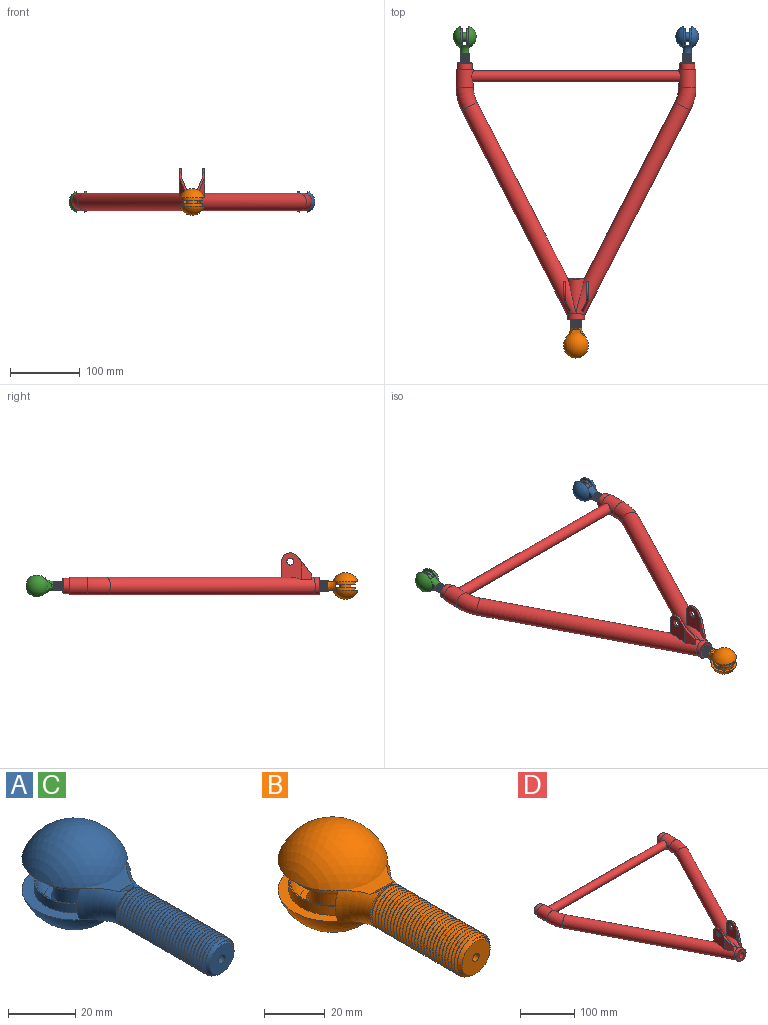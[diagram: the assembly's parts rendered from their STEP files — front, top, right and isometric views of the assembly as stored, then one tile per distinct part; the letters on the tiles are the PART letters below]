
ASSEMBLY  parts=4 mates=7
PART A: 88 faces, bbox 67.8x97.3x67.8 mm
  f0: cylinder r=12.03mm len=24.05mm, axis (0,0,1), area 245.9mm2, adj f1,f87
  f1: plane 30.08x30.08mm, normal (0,0,-1), area 28.6mm2, adj f0,f2
  f2: sphere r=11.91mm, area 421.7mm2, adj f1,f3
  f3: plane 17.75x17.75mm, normal (0,0,-1), area 94.1mm2, adj f2,f4
  f4: cone r=0mm half-angle=45deg, axis (0,0,-1), area 37.6mm2, adj f3,f5
  f5: cylinder r=6.35mm len=14.61mm, axis (0,0,1), area 582.7mm2, adj f4,f6
  f6: cone r=0mm half-angle=45deg, axis (0,0,1), area 37.6mm2, adj f5,f7
  f7: plane 37.19x37.19mm, normal (0,0,1), area 94.1mm2, adj f6,f8
  f8: sphere r=11.91mm, area 718.6mm2, adj f7,f9
  f9: plane 30.08x30.08mm, normal (0,0,1), area 28.6mm2, adj f8,f10
  f10: cylinder r=12.03mm len=24.05mm, axis (0,0,1), area 245.9mm2, adj f9,f11
  f11: plane 37.68x31.81mm, normal (0,0,1), area 376.1mm2, adj f10,f12,f84,f85,f86
  f12: torus R=22.32mm, axis (0,-1,0), area 180.4mm2, adj f11,f13,f15,f84,f86,f87
  f13: plane 6.9x3.09mm, normal (0,0.25,-0.97), area 9.3mm2, adj f12,f14,f87
  f14: torus R=22.32mm, axis (0,-1,0), area 90.2mm2, adj f13,f15,f84,f85,f87
  f15: plane 13.2x13.2mm, normal (0,-1,0), area 15.6mm2, adj f12,f14,f16,f82,f83,f85
  f16: bspline ~38.84x12.7mm, area 1026.5mm2, adj f15,f17,f18,f19,f20,f21,f22,f23
  f17: cylinder r=6.35mm len=12.7mm, axis (0,1,0), area 2.8mm2, adj f16,f18,f83,f85
  f18: cylinder r=6.35mm len=12.7mm, axis (0,1,0), area 3.2mm2, adj f16,f17,f19,f83
  f19: cylinder r=6.35mm len=12.7mm, axis (0,1,0), area 3.2mm2, adj f16,f18,f20,f83
  f20: cylinder r=6.35mm len=12.7mm, axis (0,1,0), area 3.2mm2, adj f16,f19,f21,f83
  f21: cylinder r=6.35mm len=12.7mm, axis (0,1,0), area 3.2mm2, adj f16,f20,f22,f83
  f22: cylinder r=6.35mm len=12.7mm, axis (0,1,0), area 3.2mm2, adj f16,f21,f23,f83
  f23: cylinder r=6.35mm len=12.7mm, axis (0,1,0), area 3.2mm2, adj f16,f22,f24,f83
  f24: cylinder r=6.35mm len=12.7mm, axis (0,1,0), area 3.2mm2, adj f16,f23,f25,f83
  f25: cylinder r=6.35mm len=12.7mm, axis (0,1,0), area 3.2mm2, adj f16,f24,f26,f83
  f26: cylinder r=6.35mm len=12.7mm, axis (0,1,0), area 3.2mm2, adj f16,f25,f27,f83
  f27: cylinder r=6.35mm len=12.7mm, axis (0,1,0), area 3.2mm2, adj f16,f26,f28,f83
  f28: cylinder r=6.35mm len=12.7mm, axis (0,1,0), area 3.2mm2, adj f16,f27,f29,f83
  f29: cylinder r=6.35mm len=12.7mm, axis (0,1,0), area 3.2mm2, adj f16,f28,f30,f83
  f30: cylinder r=6.35mm len=12.7mm, axis (0,1,0), area 3.2mm2, adj f16,f29,f31,f83
  f31: cylinder r=6.35mm len=12.7mm, axis (0,1,0), area 3.2mm2, adj f16,f30,f32,f83
  f32: cylinder r=6.35mm len=12.7mm, axis (0,1,0), area 3.2mm2, adj f16,f31,f33,f83
  f33: cylinder r=6.35mm len=12.7mm, axis (0,1,0), area 3.2mm2, adj f16,f32,f34,f83
  f34: cylinder r=6.35mm len=12.7mm, axis (0,1,0), area 3.2mm2, adj f16,f33,f35,f83
  f35: cylinder r=6.35mm len=12.7mm, axis (0,1,0), area 3.2mm2, adj f16,f34,f36,f83
  f36: cylinder r=6.35mm len=12.7mm, axis (0,1,0), area 3.2mm2, adj f16,f35,f37,f83
  f37: cylinder r=6.35mm len=12.7mm, axis (0,1,0), area 3.2mm2, adj f16,f36,f38,f83
  f38: cylinder r=6.35mm len=12.7mm, axis (0,1,0), area 3.2mm2, adj f16,f37,f39,f83
  f39: cylinder r=6.35mm len=12.7mm, axis (0,1,0), area 3.2mm2, adj f16,f38,f40,f83
  f40: cylinder r=6.35mm len=12.7mm, axis (0,1,0), area 3.2mm2, adj f16,f39,f41,f83
  f41: cylinder r=6.35mm len=12.7mm, axis (0,1,0), area 3.2mm2, adj f16,f40,f42,f83
  f42: cylinder r=6.35mm len=12.7mm, axis (0,1,0), area 3.2mm2, adj f16,f41,f43,f83
  f43: cylinder r=6.35mm len=12.7mm, axis (0,1,0), area 3.2mm2, adj f16,f42,f44,f83
  f44: cylinder r=6.35mm len=12.7mm, axis (0,1,0), area 3.2mm2, adj f16,f43,f45,f83
  f45: cylinder r=6.35mm len=12.7mm, axis (0,1,0), area 3.2mm2, adj f16,f44,f46,f83
  f46: cylinder r=6.35mm len=12.7mm, axis (0,1,0), area 3.2mm2, adj f16,f45,f47,f83
  f47: cylinder r=6.35mm len=12.7mm, axis (0,1,0), area 3.2mm2, adj f16,f46,f48,f83
  f48: cylinder r=6.35mm len=12.7mm, axis (0,1,0), area 3.2mm2, adj f16,f47,f49,f83
  f49: cylinder r=6.35mm len=12.7mm, axis (0,1,0), area 3.2mm2, adj f16,f48,f50,f83
  f50: cylinder r=6.35mm len=12.7mm, axis (0,1,0), area 3.2mm2, adj f16,f49,f51,f83
  f51: cylinder r=6.35mm len=12.7mm, axis (0,1,0), area 3.2mm2, adj f16,f50,f52,f83
  f52: cylinder r=6.35mm len=12.7mm, axis (0,1,0), area 3.2mm2, adj f16,f51,f53,f83
  f53: cylinder r=6.35mm len=12.7mm, axis (0,1,0), area 3.2mm2, adj f16,f52,f54,f83
  f54: cylinder r=6.35mm len=12.7mm, axis (0,1,0), area 3.2mm2, adj f16,f53,f55,f83
  f55: cylinder r=6.35mm len=12.7mm, axis (0,1,0), area 3.2mm2, adj f16,f54,f56,f83
  f56: cylinder r=6.35mm len=12.7mm, axis (0,1,0), area 3.2mm2, adj f16,f55,f57,f83
  f57: cylinder r=6.35mm len=12.7mm, axis (0,1,0), area 3.2mm2, adj f16,f56,f58,f83
  f58: cylinder r=6.35mm len=12.7mm, axis (0,1,0), area 3.2mm2, adj f16,f57,f59,f83
  f59: cylinder r=6.35mm len=12.7mm, axis (0,1,0), area 3.2mm2, adj f16,f58,f60,f83
  f60: cylinder r=6.35mm len=12.7mm, axis (0,1,0), area 3.2mm2, adj f16,f59,f61,f83
  f61: cylinder r=6.35mm len=12.7mm, axis (0,1,0), area 3.2mm2, adj f16,f60,f62,f83
  f62: cylinder r=6.35mm len=12.7mm, axis (0,1,0), area 3.2mm2, adj f16,f61,f63,f83
  f63: cylinder r=6.35mm len=12.7mm, axis (0,1,0), area 3.2mm2, adj f16,f62,f64,f83
  f64: cylinder r=6.35mm len=12.7mm, axis (0,1,0), area 3.2mm2, adj f16,f63,f65,f83
  f65: cylinder r=6.35mm len=12.7mm, axis (0,1,0), area 3.2mm2, adj f16,f64,f66,f83
  f66: cylinder r=6.35mm len=12.7mm, axis (0,1,0), area 3.2mm2, adj f16,f65,f67,f83
  f67: cylinder r=6.35mm len=12.7mm, axis (0,1,0), area 3.2mm2, adj f16,f66,f68,f83
  f68: cylinder r=6.35mm len=12.7mm, axis (0,1,0), area 3.2mm2, adj f16,f67,f69,f83
  f69: cylinder r=6.35mm len=12.7mm, axis (0,1,0), area 3.2mm2, adj f16,f68,f70,f83
  f70: cylinder r=6.35mm len=12.7mm, axis (0,1,0), area 3.2mm2, adj f16,f69,f71,f83
  f71: cylinder r=6.35mm len=12.7mm, axis (0,1,0), area 3.2mm2, adj f16,f70,f72,f83
  f72: cylinder r=6.35mm len=12.7mm, axis (0,1,0), area 3.2mm2, adj f16,f71,f73,f83
  f73: cylinder r=6.35mm len=12.7mm, axis (0,1,0), area 3.2mm2, adj f16,f72,f74,f76,f83
  f74: cylinder r=6.35mm len=12.7mm, axis (0,1,0), area 3.2mm2, adj f73,f75,f76,f83
  f75: cylinder r=6.35mm len=4.49mm, axis (0,1,0), area 0.4mm2, adj f74,f76,f81
  f76: bspline ~14.55x14.53mm, area 18.3mm2, adj f73,f74,f75,f77,f81
  f77: cone r=0mm half-angle=45deg, axis (0,1,0), area 18.6mm2, adj f76,f78,f81
  f78: plane 10.16x10.16mm, normal (0,-1,0), area 74mm2, adj f77,f79,f81
  f79: cylinder r=1.5mm len=15mm, axis (0,-1,0), area 141.4mm2, adj f78,f80
  f80: plane 3x3mm, normal (0,-1,0), area 7.1mm2, adj f79
  f81: cone r=0mm half-angle=45deg, axis (0,1,0), area 23.7mm2, adj f16,f75,f76,f77,f78,f82,f83
  f82: cylinder r=5.53mm len=37.66mm, axis (0,1,0), area 165.1mm2, adj f15,f16,f81,f83
  f83: bspline ~38.26x12.7mm, area 1045.6mm2, adj f15,f17,f18,f19,f20,f21,f22,f23
  f84: sphere r=16.67mm, area 2557.4mm2, adj f11,f12,f14,f85,f87
  f85: torus R=22.32mm, axis (0,-1,0), area 90.2mm2, adj f11,f14,f15,f17,f84,f86
  f86: plane 6.9x3.09mm, normal (0,0.25,0.97), area 9.3mm2, adj f11,f12,f85
  f87: plane 37.68x31.81mm, normal (0,0,-1), area 376.3mm2, adj f0,f12,f13,f14,f84
PART B: 86 faces, bbox 74.1x108.1x74.1 mm
  f0: cylinder r=14.43mm len=28.86mm, axis (0,0,1), area 331.1mm2, adj f1,f2
  f1: plane 41.2x36.29mm, normal (0,0,-1), area 441.4mm2, adj f0,f3,f4,f5,f6
  f2: plane 35.07x35.07mm, normal (0,0,-1), area 32.5mm2, adj f0,f7
  f3: sphere r=19.05mm, area 3418.5mm2, adj f1,f4,f6,f8,f9
  f4: torus R=23.47mm, axis (0,-1,0), area 92.7mm2, adj f1,f3,f5,f8,f10,f11
  f5: plane 11.68x3.5mm, normal (0,0.59,-0.81), area 21.6mm2, adj f1,f4,f6
  f6: torus R=23.47mm, axis (0,-1,0), area 185.4mm2, adj f1,f3,f5,f9,f10,f12
  f7: sphere r=14.29mm, area 649.9mm2, adj f2,f13
  f8: torus R=23.47mm, axis (0,-1,0), area 92.7mm2, adj f3,f4,f9,f10,f12
  f9: plane 41.19x36.28mm, normal (0,0,1), area 441.4mm2, adj f3,f6,f8,f12,f14
  f10: plane 16.47x16.47mm, normal (0,-1,0), area 21.8mm2, adj f4,f6,f8,f15,f16,f17
  f11: cylinder r=7.94mm len=7.85mm, axis (0,1,0), area 1.4mm2, adj f4,f15,f17,f18
  f12: plane 11.68x3.5mm, normal (0,0.59,0.81), area 21.6mm2, adj f6,f8,f9
  f13: plane 21.3x21.3mm, normal (0,0,-1), area 116.8mm2, adj f7,f19
  f14: cylinder r=14.43mm len=28.86mm, axis (0,0,1), area 331.1mm2, adj f9,f20
  f15: bspline ~41.48x15.88mm, area 1421.3mm2, adj f10,f11,f16,f18,f21,f22,f23,f24
  f16: cylinder r=7.02mm len=40.78mm, axis (0,-1,0), area 224.7mm2, adj f10,f15,f17,f21
  f17: bspline ~41.84x15.87mm, area 1394.1mm2, adj f10,f11,f16,f18,f21,f22,f23,f24
  f18: cylinder r=7.94mm len=15.88mm, axis (0,1,0), area 4.4mm2, adj f11,f15,f17,f22
  f19: cone r=0mm half-angle=45deg, axis (0,0,-1), area 58.8mm2, adj f13,f79
  f20: plane 35.07x35.07mm, normal (0,0,1), area 32.5mm2, adj f14,f80
  f21: cone r=0mm half-angle=45deg, axis (0,1,0), area 33.4mm2, adj f15,f16,f17,f77,f78,f81
  f22: cylinder r=7.94mm len=15.88mm, axis (0,1,0), area 4.4mm2, adj f15,f17,f18,f23
  f23: cylinder r=7.94mm len=15.88mm, axis (0,1,0), area 4.4mm2, adj f15,f17,f22,f24
  f24: cylinder r=7.94mm len=15.88mm, axis (0,1,0), area 4.4mm2, adj f15,f17,f23,f25
  f25: cylinder r=7.94mm len=15.88mm, axis (0,1,0), area 4.4mm2, adj f15,f17,f24,f26
  f26: cylinder r=7.94mm len=15.88mm, axis (0,1,0), area 4.4mm2, adj f15,f17,f25,f27
  f27: cylinder r=7.94mm len=15.88mm, axis (0,1,0), area 4.4mm2, adj f15,f17,f26,f28
  f28: cylinder r=7.94mm len=15.88mm, axis (0,1,0), area 4.4mm2, adj f15,f17,f27,f29
  f29: cylinder r=7.94mm len=15.88mm, axis (0,1,0), area 4.4mm2, adj f15,f17,f28,f30
  f30: cylinder r=7.94mm len=15.88mm, axis (0,1,0), area 4.4mm2, adj f15,f17,f29,f31
  f31: cylinder r=7.94mm len=15.88mm, axis (0,1,0), area 4.4mm2, adj f15,f17,f30,f32
  f32: cylinder r=7.94mm len=15.88mm, axis (0,1,0), area 4.4mm2, adj f15,f17,f31,f33
  f33: cylinder r=7.94mm len=15.88mm, axis (0,1,0), area 4.4mm2, adj f15,f17,f32,f34
  f34: cylinder r=7.94mm len=15.88mm, axis (0,1,0), area 4.4mm2, adj f15,f17,f33,f35
  f35: cylinder r=7.94mm len=15.88mm, axis (0,1,0), area 4.4mm2, adj f15,f17,f34,f36
  f36: cylinder r=7.94mm len=15.88mm, axis (0,1,0), area 4.4mm2, adj f15,f17,f35,f37
  f37: cylinder r=7.94mm len=15.88mm, axis (0,1,0), area 4.4mm2, adj f15,f17,f36,f38
  f38: cylinder r=7.94mm len=15.88mm, axis (0,1,0), area 4.4mm2, adj f15,f17,f37,f39
  f39: cylinder r=7.94mm len=15.88mm, axis (0,1,0), area 4.4mm2, adj f15,f17,f38,f40
  f40: cylinder r=7.94mm len=15.88mm, axis (0,1,0), area 4.4mm2, adj f15,f17,f39,f41
  f41: cylinder r=7.94mm len=15.88mm, axis (0,1,0), area 4.4mm2, adj f15,f17,f40,f42
  f42: cylinder r=7.94mm len=15.88mm, axis (0,1,0), area 4.4mm2, adj f15,f17,f41,f43
  f43: cylinder r=7.94mm len=15.88mm, axis (0,1,0), area 4.4mm2, adj f15,f17,f42,f44
  f44: cylinder r=7.94mm len=15.88mm, axis (0,1,0), area 4.4mm2, adj f15,f17,f43,f45
  f45: cylinder r=7.94mm len=15.88mm, axis (0,1,0), area 4.4mm2, adj f15,f17,f44,f46
  f46: cylinder r=7.94mm len=15.88mm, axis (0,1,0), area 4.4mm2, adj f15,f17,f45,f47
  f47: cylinder r=7.94mm len=15.88mm, axis (0,1,0), area 4.4mm2, adj f15,f17,f46,f48
  f48: cylinder r=7.94mm len=15.88mm, axis (0,1,0), area 4.4mm2, adj f15,f17,f47,f49
  f49: cylinder r=7.94mm len=15.88mm, axis (0,1,0), area 4.4mm2, adj f15,f17,f48,f50
  f50: cylinder r=7.94mm len=15.88mm, axis (0,1,0), area 4.4mm2, adj f15,f17,f49,f51
  f51: cylinder r=7.94mm len=15.88mm, axis (0,1,0), area 4.4mm2, adj f15,f17,f50,f52
  f52: cylinder r=7.94mm len=15.88mm, axis (0,1,0), area 4.4mm2, adj f15,f17,f51,f53
  f53: cylinder r=7.94mm len=15.88mm, axis (0,1,0), area 4.4mm2, adj f15,f17,f52,f54
  f54: cylinder r=7.94mm len=15.88mm, axis (0,1,0), area 4.4mm2, adj f15,f17,f53,f55
  f55: cylinder r=7.94mm len=15.88mm, axis (0,1,0), area 4.4mm2, adj f15,f17,f54,f56
  f56: cylinder r=7.94mm len=15.88mm, axis (0,1,0), area 4.4mm2, adj f15,f17,f55,f57
  f57: cylinder r=7.94mm len=15.88mm, axis (0,1,0), area 4.4mm2, adj f15,f17,f56,f58
  f58: cylinder r=7.94mm len=15.88mm, axis (0,1,0), area 4.4mm2, adj f15,f17,f57,f59
  f59: cylinder r=7.94mm len=15.88mm, axis (0,1,0), area 4.4mm2, adj f15,f17,f58,f60
  f60: cylinder r=7.94mm len=15.88mm, axis (0,1,0), area 4.4mm2, adj f15,f17,f59,f61
  f61: cylinder r=7.94mm len=15.88mm, axis (0,1,0), area 4.4mm2, adj f15,f17,f60,f62
  f62: cylinder r=7.94mm len=15.88mm, axis (0,1,0), area 4.4mm2, adj f15,f17,f61,f63
  f63: cylinder r=7.94mm len=15.88mm, axis (0,1,0), area 4.4mm2, adj f15,f17,f62,f64
  f64: cylinder r=7.94mm len=15.88mm, axis (0,1,0), area 4.4mm2, adj f15,f17,f63,f65
  f65: cylinder r=7.94mm len=15.88mm, axis (0,1,0), area 4.4mm2, adj f15,f17,f64,f66
  f66: cylinder r=7.94mm len=15.88mm, axis (0,1,0), area 4.4mm2, adj f15,f17,f65,f67
  f67: cylinder r=7.94mm len=15.88mm, axis (0,1,0), area 4.4mm2, adj f15,f17,f66,f68
  f68: cylinder r=7.94mm len=15.88mm, axis (0,1,0), area 4.4mm2, adj f15,f17,f67,f69
  f69: cylinder r=7.94mm len=15.88mm, axis (0,1,0), area 4.4mm2, adj f15,f17,f68,f70
  f70: cylinder r=7.94mm len=15.88mm, axis (0,1,0), area 4.4mm2, adj f15,f17,f69,f71
  f71: cylinder r=7.94mm len=15.88mm, axis (0,1,0), area 4.4mm2, adj f15,f17,f70,f72
  f72: cylinder r=7.94mm len=15.88mm, axis (0,1,0), area 4.4mm2, adj f15,f17,f71,f73
  f73: cylinder r=7.94mm len=15.88mm, axis (0,1,0), area 4.4mm2, adj f15,f17,f72,f74
  f74: cylinder r=7.94mm len=15.88mm, axis (0,1,0), area 4.4mm2, adj f15,f17,f73,f75
  f75: cylinder r=7.94mm len=15.88mm, axis (0,1,0), area 4.4mm2, adj f15,f17,f74,f76
  f76: cylinder r=7.94mm len=15.88mm, axis (0,1,0), area 4.4mm2, adj f15,f17,f75,f78
  f77: cone r=0mm half-angle=45deg, axis (0,1,0), area 26.4mm2, adj f17,f21,f81
  f78: cylinder r=7.94mm len=5.61mm, axis (0,1,0), area 0.6mm2, adj f17,f21,f76
  f79: cylinder r=7.94mm len=17.46mm, axis (0,0,1), area 870.9mm2, adj f19,f82
  f80: sphere r=14.29mm, area 1077.4mm2, adj f20,f83
  f81: plane 13.05x13.05mm, normal (0,-1,0), area 126.7mm2, adj f21,f77,f84
  f82: cone r=0mm half-angle=45deg, axis (0,0,1), area 58.8mm2, adj f79,f83
  f83: plane 44.63x44.63mm, normal (0,0,1), area 116.8mm2, adj f80,f82
  f84: cylinder r=1.5mm len=20mm, axis (0,-1,0), area 188.5mm2, adj f81,f85
  f85: plane 3x3mm, normal (0,-1,0), area 7.1mm2, adj f84
PART C: same geometry as A
PART D: 57 faces, bbox 357x370x60 mm
  f0: plane 37.36x27.93mm, normal (-1,0,0), area 818.5mm2, adj f22,f40,f42,f50,f51,f53
  f1: plane 38.34x28.66mm, normal (-1,0,0), area 840.4mm2, adj f4,f46,f47,f48,f49,f52
  f2: plane 37.36x27.93mm, normal (1,0,0), area 818.5mm2, adj f4,f44,f46,f48,f49,f52
  f3: plane 38.34x28.66mm, normal (1,0,0), area 840.4mm2, adj f22,f42,f43,f50,f51,f53
  f4: cylinder r=12.5mm len=308.52mm, axis (0.46,-0.89,0), area 24749.2mm2, adj f1,f2,f7,f23,f24,f26,f27,f44
  f5: cylinder r=12.5mm len=25.43mm, axis (0,-1,0), area 1787.4mm2, adj f27,f28,f39
  f6: cylinder r=12.5mm len=25.43mm, axis (0,-1,0), area 1787mm2, adj f20,f21,f39
  f7: cylinder r=12.5mm len=50mm, axis (0,-1,0), area 662.4mm2, adj f4,f22,f23,f37,f38
  f8: plane 21x21mm, normal (0,-1,0), area 242.3mm2, adj f12,f13
  f9: cylinder r=12.5mm len=45.79mm, axis (0,-1,0), area 851.3mm2, adj f10
  f10: cylinder r=10.5mm len=300.54mm, axis (-0.46,-0.89,0), area 20636.2mm2, adj f9,f11
  f11: torus R=60mm, axis (0,0,-1), area 1886.1mm2, adj f10,f12
  f12: cylinder r=10.5mm len=21mm, axis (0,-1,0), area 1017.9mm2, adj f8,f11
  f13: cylinder r=5.75mm len=20mm, axis (0,1,0), area 723.1mm2, adj f8,f29
  f14: plane 21x21mm, normal (0,-1,0), area 242.3mm2, adj f18,f19
  f15: cylinder r=12.5mm len=45.79mm, axis (0,-1,0), area 851.3mm2, adj f16
  f16: cylinder r=10.5mm len=300.54mm, axis (0.46,-0.89,0), area 20636.2mm2, adj f15,f17
  f17: torus R=60mm, axis (0,0,-1), area 1886.1mm2, adj f16,f18
  f18: cylinder r=10.5mm len=21mm, axis (0,-1,0), area 1017.9mm2, adj f14,f17
  f19: cylinder r=5.75mm len=20mm, axis (0,1,0), area 723.1mm2, adj f14,f32
  f20: plane 25x25mm, normal (0,1,0), area 110.7mm2, adj f6,f30
  f21: torus R=60mm, axis (0,0,-1), area 2245.3mm2, adj f6,f22
  f22: cylinder r=12.5mm len=308.52mm, axis (-0.46,-0.89,0), area 24749.2mm2, adj f0,f3,f7,f21,f23,f24,f26,f40
  f23: plane 24.28x24mm, normal (0,1,0), area 335.3mm2, adj f4,f7,f22,f24,f36,f37
  f24: cylinder r=12.5mm len=50mm, axis (0,-1,0), area 682.6mm2, adj f4,f22,f23
  f25: plane 23x23mm, normal (0,-1,0), area 272.5mm2, adj f35,f36
  f26: cylinder r=12.5mm len=25mm, axis (0,-1,0), area 555.1mm2, adj f4,f22,f35
  f27: torus R=60mm, axis (0,0,-1), area 2245.3mm2, adj f4,f5
  f28: plane 25x25mm, normal (0,1,0), area 110.7mm2, adj f5,f31
  f29: plane 20x20mm, normal (0,1,0), area 210.1mm2, adj f13,f34
  f30: cylinder r=11mm len=22mm, axis (0,1,0), area 622mm2, adj f20,f34
  f31: cylinder r=11mm len=22mm, axis (0,1,0), area 622mm2, adj f28,f33
  f32: plane 20x20mm, normal (0,1,0), area 210.1mm2, adj f19,f33
  f33: cone r=11mm half-angle=45deg, axis (0,-1,0), area 93.3mm2, adj f31,f32
  f34: cone r=11mm half-angle=45deg, axis (0,-1,0), area 93.3mm2, adj f29,f30
  f35: cone r=11.5mm half-angle=45deg, axis (0,1,0), area 106.6mm2, adj f25,f26
  f36: cylinder r=6.75mm len=60mm, axis (0,-1,0), area 2543.3mm2, adj f23,f25
  f37: plane 9.8x2mm, normal (0,0,1), area 19.6mm2, adj f7,f23,f38
  f38: plane 9.8x1mm, normal (0,1,0), area 6.6mm2, adj f7,f37
  f39: cylinder r=7.94mm len=300.69mm, axis (-1,0,0), area 14849.6mm2, adj f5,f6
  f40: plane 24.43x14.19mm, normal (-0.89,0.46,0), area 246.9mm2, adj f0,f22,f41,f50
  f41: plane 8.57x2.67mm, normal (-0.46,-0.89,0), area 19.7mm2, adj f22,f40,f43,f50
  f42: plane 24.91x3.05mm, normal (0,1,0), area 72.2mm2, adj f0,f3,f22,f51
  f43: plane 25.57x14.83mm, normal (0.89,-0.46,0), area 270.4mm2, adj f3,f22,f41,f50
  f44: plane 24.43x14.19mm, normal (0.89,0.46,0), area 246.9mm2, adj f2,f4,f45,f48
  f45: plane 8.57x2.67mm, normal (0.46,-0.89,0), area 19.7mm2, adj f4,f44,f47,f48
  f46: plane 24.91x3.05mm, normal (0,1,0), area 72.2mm2, adj f1,f2,f4,f49
  f47: plane 25.57x14.83mm, normal (-0.89,-0.46,0), area 270.4mm2, adj f1,f4,f45,f48
  f48: plane 26.76x21.19mm, normal (0,-0.78,0.62), area 107.9mm2, adj f1,f2,f44,f45,f47,f49
  f49: cylinder r=12.5mm len=22.3mm, axis (1,0,0), area 92.7mm2, adj f1,f2,f46,f48
  f50: plane 26.76x21.19mm, normal (0,-0.78,0.62), area 107.9mm2, adj f0,f3,f40,f41,f43,f51
  f51: cylinder r=12.5mm len=22.3mm, axis (1,0,0), area 92.7mm2, adj f0,f3,f42,f50
  f52: cylinder r=5.1mm len=10.2mm, axis (1,0,0), area 96.1mm2, adj f1,f2
  f53: cylinder r=5.1mm len=10.2mm, axis (1,0,0), area 96.1mm2, adj f0,f3
  f54: cylinder r=12.5mm len=12.88mm, axis (0,-1,0), area 135mm2, adj f56
  f55: cylinder r=12.5mm len=12.88mm, axis (0,-1,0), area 134.9mm2, adj f56
  f56: cylinder r=6.44mm len=298.57mm, axis (-1,0,0), area 12003mm2, adj f54,f55
PLACE A rot(axis=(0,1,0),90deg) t=(160,23.1,0)mm
PLACE B rot(axis=(1,0,0),180deg) t=(0,-371.28,0)mm
PLACE C rot(axis=(0,1,0),90deg) t=(-160,23.1,0)mm
PLACE D at identity fixed
MATE planar D.f5 <-> C.f17  axis (0,1,0) through (-160,10,0)mm
MATE cylindrical A.f0 <-> C.f0  axis (1,0,0) through (167.3,46.91,0)mm
MATE planar D.f7 <-> B.f84  axis (0,-1,0) through (0,-360,0)mm
MATE cylindrical A.f79 <-> D.f13  axis (0,-1,0) through (160,-7.5,0)mm
MATE parallel B.f0 <-> D.f37  axis (0,0,1) through (0,-396.68,9.52)mm
MATE cylindrical B.f84 <-> D.f36  axis (0,1,0) through (0,-340,0)mm
MATE cylindrical D.f19 <-> C.f79  axis (0,1,0) through (-160,10,0)mm
